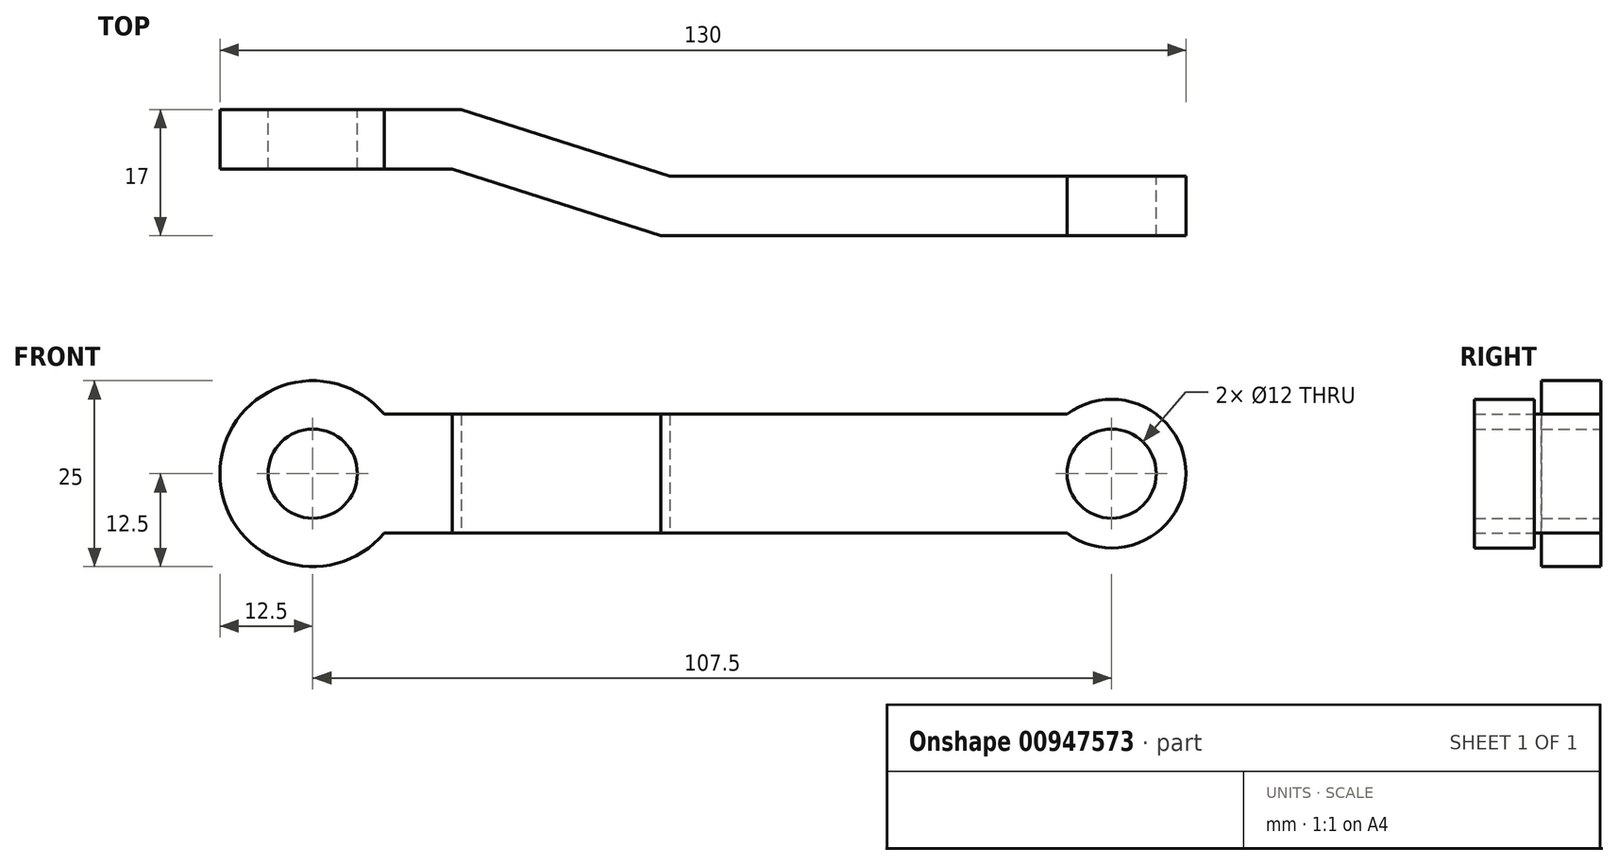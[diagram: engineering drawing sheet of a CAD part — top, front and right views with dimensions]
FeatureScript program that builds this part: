
annotation { "Feature Type Name" : "Feature", "Feature Type Description" : "" }
export const myFeature = defineFeature(function(context is Context, id is Id, definition is map)
    precondition{}
    {
        {
            var Q0;
            Q0=qCreatedBy(makeId("Front.planeOp"),FACE);
            var sketch = newSketch(context, id + "F0", { "sketchPlane" : qUnion([Q0])});
            skCircle(sketch, "E0", {"center": v(0, 0) * mm, "radius": 12.5 * mm});
            skCircle(sketch, "E1", {"center": v(107.5, 0) * mm, "radius": 10 * mm});
            skLineSegment(sketch, "E2", {"start": v(12.5, 0) * mm, "end": v(97.5, 0) * mm, "construction": true});
            skLineSegment(sketch, "E3", {"start": v(9.6, 8) * mm, "end": v(101.5, 8) * mm});
            skLineSegment(sketch, "E4.MirrorCS", {"start": v(9.6, -8) * mm, "end": v(101.5, -8) * mm});
            skCircle(sketch, "E5", {"center": v(0, 0) * mm, "radius": 6 * mm});
            skCircle(sketch, "E6", {"center": v(107.5, 0) * mm, "radius": 6 * mm});
            skSolve(sketch);
        }
        {
            var Q0;
            Q0 = qSketchRegion(id + "F0", true);
            extrude(context, id + "F1", {"entities" : qUnion([Q0]), "depth" : 25 * mm, "offsetDistance" : 25 * mm});
        }
        {
            var Q0;
            Q0=qCreatedBy(makeId("Top.planeOp"),FACE);
            var sketch = newSketch(context, id + "F2", { "sketchPlane" : qUnion([Q0])});
            skLineSegment(sketch, "E7", {"start": v(-12.5, 0) * mm, "end": v(20, 0) * mm});
            skLineSegment(sketch, "E8", {"start": v(20, 0) * mm, "end": v(48.05, -9) * mm});
            skLineSegment(sketch, "E9", {"start": v(48.05, -9) * mm, "end": v(117.5, -9) * mm});
            skLineSegment(sketch, "E10.0", {"start": v(46.8, -17) * mm, "end": v(117.5, -17) * mm});
            skLineSegment(sketch, "E10.1", {"start": v(18.75, -8) * mm, "end": v(46.8, -17) * mm});
            skLineSegment(sketch, "E10.2", {"start": v(-12.5, -8) * mm, "end": v(18.75, -8) * mm});
            skLineSegment(sketch, "E11", {"start": v(117.5, -9) * mm, "end": v(117.5, -17) * mm});
            skLineSegment(sketch, "E12", {"start": v(-12.5, 0) * mm, "end": v(-12.5, -8) * mm});
            skLineSegment(sketch, "E13", {"start": v(117.5, 0) * mm, "end": v(117.5, -25) * mm});
            skLineSegment(sketch, "E14", {"start": v(-12.5, -25) * mm, "end": v(-12.5, 0) * mm});
            skSolve(sketch);
        }
        {
            var Q0;
            Q0=makeQuery(id+"F2.imprint","IMPRINT",FACE,{"disambiguationData":[TD([[makeQuery(id+"F2.imprint","IMPRINT",EDGE,{"derivedFrom":sQuery(id+"F2.wireOp",EDGE,"E7")}),-1.0]])]});
            extrude(context, id + "F3", {"entities" : qUnion([Q0]), "operationType" : NewBodyOperationType.INTERSECT, "endBound" : BoundingType.SYMMETRIC, "depth" : 25 * mm, "offsetDistance" : 25 * mm});
        }
    });
